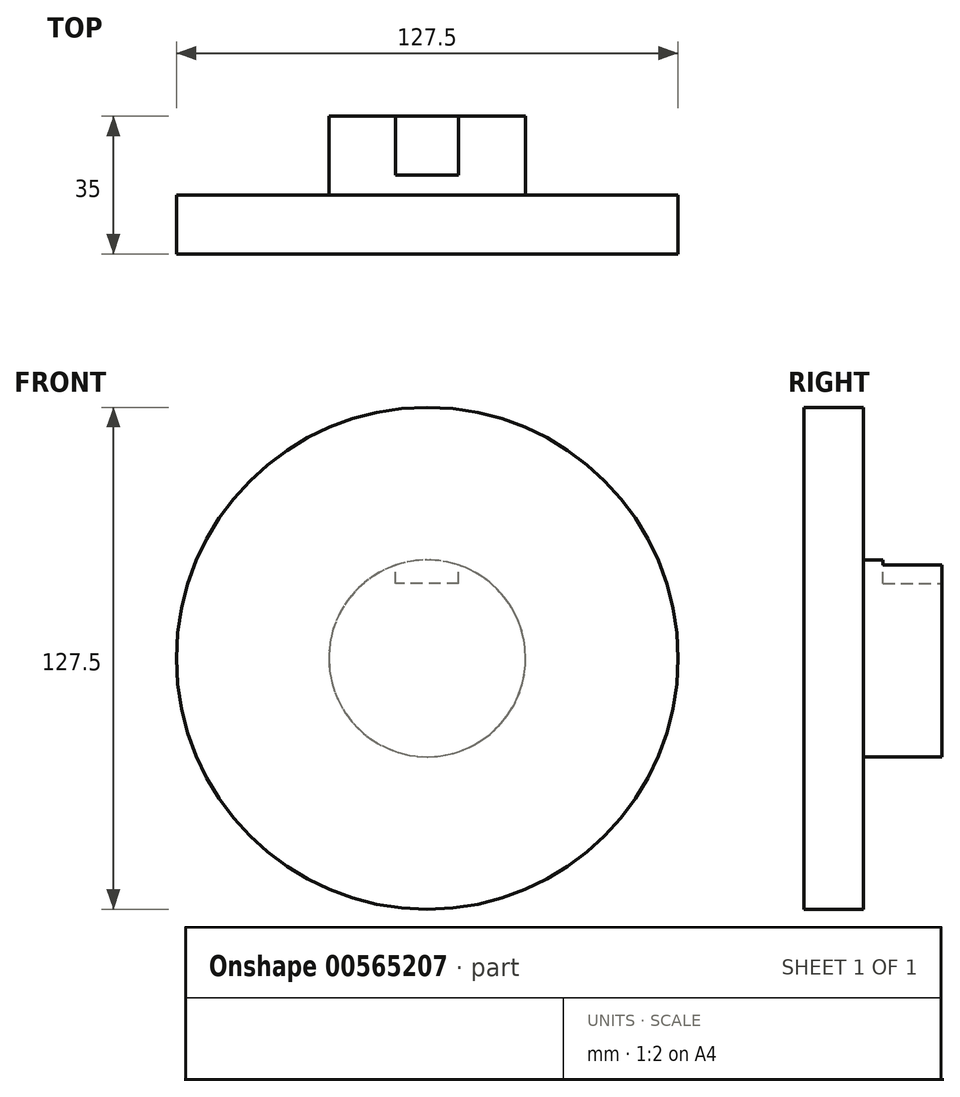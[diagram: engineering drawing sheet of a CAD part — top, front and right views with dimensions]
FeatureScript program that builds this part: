
annotation { "Feature Type Name" : "Feature", "Feature Type Description" : "" }
export const myFeature = defineFeature(function(context is Context, id is Id, definition is map)
    precondition{}
    {
        {
            var Q0;
            Q0=qCreatedBy(makeId("Front.planeOp"),FACE);
            var sketch = newSketch(context, id + "F0", { "sketchPlane" : qUnion([Q0])});
            skCircle(sketch, "E0", {"center": v(0, 0) * mm, "radius": 63.75 * mm});
            skCircle(sketch, "E1", {"center": v(0, 0) * mm, "radius": 70 * mm, "construction": true});
            skCircle(sketch, "E2", {"center": v(0, 0) * mm, "radius": 75 * mm, "construction": true});
            skLineSegment(sketch, "E3", {"start": v(0, 0) * mm, "end": v(0, 142.53) * mm, "construction": true});
            skLineSegment(sketch, "E4", {"start": v(0, 0) * mm, "end": v(-8.3, 147.71) * mm, "construction": true});
            skLineSegment(sketch, "E5", {"start": v(0, 70) * mm, "end": v(-109.9, 70) * mm, "construction": true});
            skLineSegment(sketch, "E6", {"start": v(0, 70) * mm, "end": v(-107.13, 31) * mm, "construction": true});
            skCircle(sketch, "E7", {"center": v(0, 0) * mm, "radius": 65.78 * mm, "construction": true});
            skCircle(sketch, "E8", {"center": v(0, 70) * mm, "radius": 17.5 * mm, "construction": true});
            skCircle(sketch, "E9", {"center": v(-16.33, 63.72) * mm, "radius": 17.5 * mm, "construction": true});
            skArc(sketch, "E10", {"start": v(-2.9, 74.94) * mm, "mid": v(0.11, 69.7) * mm, "end": v(1.17, 63.74) * mm});
            skArc(sketch, "E11.MirrorCS", {"start": v(-5.5, 74.8) * mm, "mid": v(-7.91, 69.25) * mm, "end": v(-8.3, 63.2) * mm});
            skArc(sketch, "E12", {"start": v(-5.5, 74.8) * mm, "mid": v(-4.2, 74.88) * mm, "end": v(-2.9, 74.94) * mm});
            skCircle(sketch, "E13", {"center": v(0, 0) * mm, "radius": 25 * mm});
            skSolve(sketch);
        }
        {
            var Q0;
            {var subQ0=sQuery(id+"F0.wireOp",EDGE,"E0");var subQ1=makeQuery(id+"F0.imprint","INTERSECT",VERTEX,{"derivedFrom":[subQ0,sQuery(id+"F0.wireOp",EDGE,"E10")]});Q0=makeQuery(id+"F0.imprint","IMPRINT",FACE,{"disambiguationData":[TD([[makeQuery(id+"F0.imprint","IMPRINT",EDGE,{"disambiguationData":[TD([[subQ1,-1.0]])],"derivedFrom":subQ0}),1.0]])]});}
            var Q1;
            {var subQ0=sQuery(id+"F0.wireOp",EDGE,"E10");Q1=makeQuery(id+"F0.imprint","IMPRINT",FACE,{"disambiguationData":[TD([[makeQuery(id+"F0.imprint","IMPRINT",EDGE,{"derivedFrom":subQ0}),-1.0]])]});}
            var Q2;
            Q2=makeQuery(id+"F0.imprint","IMPRINT",FACE,{"disambiguationData":[TD([[makeQuery(id+"F0.imprint","IMPRINT",EDGE,{"derivedFrom":sQuery(id+"F0.wireOp",EDGE,"E13")}),1.0]])]});
            extrude(context, id + "F1", {"entities" : qUnion([Q0, Q1, Q2]), "depth" : 15 * mm, "offsetDistance" : 25.4 * mm});
        }
        {
            var Q0;
            Q0=makeQuery(id+"F1.opExtrude","SWEPT_BODY",BODY,{"disambiguationData":[OSD([sQuery(id+"F0.wireOp",EDGE,"E0"),sQuery(id+"F0.wireOp",EDGE,"E10"),sQuery(id+"F0.wireOp",EDGE,"E11.MirrorCS"),sQuery(id+"F0.wireOp",EDGE,"E12")])]});
            var Q1;
            Q1=makeQuery(id+"F1.opExtrude","SWEPT_FACE",FACE,{"disambiguationData":[OSD([sQuery(id+"F0.wireOp",EDGE,"E0")])]});
            circularPattern(context, id + "F2", {"entities" : qUnion([Q0]), "axis" : qUnion([Q1]), "angle" : 360 * degree, "instanceCount" : 28, "equalSpace" : true});
        }
        {
            var Q0;
            Q0=makeQuery(id+"F0.imprint","IMPRINT",FACE,{"disambiguationData":[TD([[makeQuery(id+"F0.imprint","IMPRINT",EDGE,{"derivedFrom":sQuery(id+"F0.wireOp",EDGE,"E13")}),1.0]])]});
            extrude(context, id + "F3", {"entities" : qUnion([Q0]), "operationType" : NewBodyOperationType.ADD, "oppositeDirection" : true, "depth" : 20 * mm, "offsetDistance" : 25.4 * mm});
        }
        {
            var Q0;
            Q0=makeQuery(id+"F3.opExtrude","CAP_FACE",FACE,{"disambiguationData":[OSD([sQuery(id+"F0.wireOp",EDGE,"E13")])],"isStart":false});
            var sketch = newSketch(context, id + "F4", { "sketchPlane" : qUnion([Q0])});
            skLineSegment(sketch, "E14.bottom", {"start": v(-8, 19) * mm, "end": v(8, 19) * mm});
            skLineSegment(sketch, "E14.top", {"start": v(-8, 39.3) * mm, "end": v(8, 39.3) * mm});
            skLineSegment(sketch, "E14.left", {"start": v(-8, 19) * mm, "end": v(-8, 39.3) * mm});
            skLineSegment(sketch, "E14.right", {"start": v(8, 19) * mm, "end": v(8, 39.3) * mm});
            skSolve(sketch);
        }
        {
            var Q0;
            Q0=qSketchRegion(id+"F4",true);
            extrude(context, id + "F5", {"entities" : qUnion([Q0]), "operationType" : NewBodyOperationType.REMOVE, "oppositeDirection" : true, "depth" : 15 * mm, "offsetDistance" : 25.4 * mm});
        }
    });
